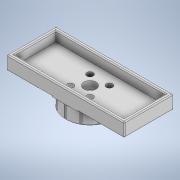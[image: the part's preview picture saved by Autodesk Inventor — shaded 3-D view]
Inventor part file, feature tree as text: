
AUTODESK INVENTOR PART (.ipt)
format: ipt  version: 2022 (Build 260153000, 153)  size: 391,680 bytes
history: native  units: mm
features: sketch x8, extrude x7, fillet x3, other x2, pattern_circular x1, revolve x1, projected_geometry x1
ambient origin geometry x8: Origin, YZ Plane, XZ Plane, XY Plane, X Axis, Y Axis, Z Axis, Center Point
bodies: Body1 (feature_tree)
feature tree (23):
  other  "Твердое тело1"
  extrude  "Выдавливание1"  Depth=20.0mm
  extrude  "Выдавливание2"  Depth=55.6mm
  sketch  "Эскиз3"
  extrude  "Выдавливание3"  Depth=2.5mm
  extrude  "Выдавливание4"  Depth=2.0mm
  sketch  "Эскиз6"
  extrude  "Выдавливание5"  Depth=2.0mm TaperAngle=0.0deg
  extrude  "Выдавливание6"  Depth=2.0mm
  extrude  "Выдавливание7"  Depth=2.0mm
  fillet  "Сопряжение2"  Radius=5.0mm
  pattern_circular  "Круговой массив1"  [2 undecoded]
  fillet  "Сопряжение3"  Radius=40.0mm
  other  "РабПлоскость1"
  revolve  "Вращение1"
  fillet  "Сопряжение4"  Radius=3.2mm
  sketch  "Эскиз1"
  sketch  "Эскиз2"
  projected_geometry  "Спроецированная петля1"
  sketch  "Эскиз4"
  sketch  "Эскиз7"
  sketch  "Эскиз8"
  sketch  "Эскиз10"
note: 2 required parameter values undecoded (feature->parameter linkage not recoverable at this tier; creation-order binding heuristic only, values carry confidence <= 0.55)
